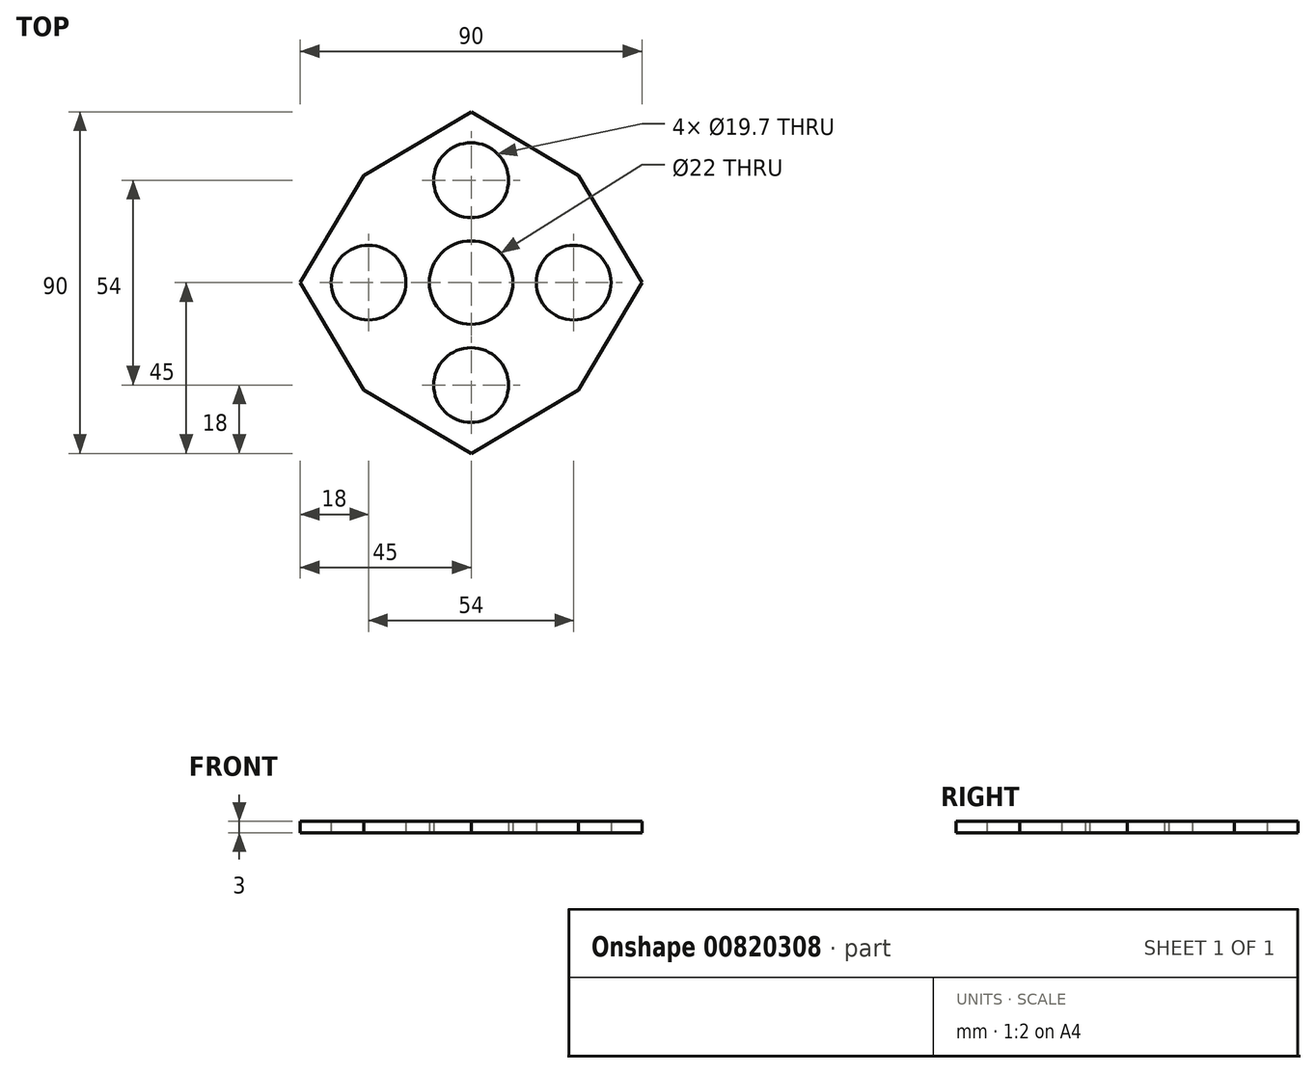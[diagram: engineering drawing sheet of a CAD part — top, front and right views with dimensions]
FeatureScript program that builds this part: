
annotation { "Feature Type Name" : "Feature", "Feature Type Description" : "" }
export const myFeature = defineFeature(function(context is Context, id is Id, definition is map)
    precondition{}
    {
        {
            var Q0;
            Q0=qCreatedBy(makeId("Top.planeOp"),FACE);
            var sketch = newSketch(context, id + "F0", { "sketchPlane" : qUnion([Q0])});
            skCircle(sketch, "E0", {"center": v(0, 0) * mm, "radius": 11 * mm});
            skLineSegment(sketch, "E1", {"start": v(-45, 0) * mm, "end": v(-28.28, 28.28) * mm});
            skLineSegment(sketch, "E2", {"start": v(-28.28, 28.28) * mm, "end": v(0, 45) * mm});
            skLineSegment(sketch, "E3", {"start": v(0, 45) * mm, "end": v(28.28, 28.28) * mm});
            skLineSegment(sketch, "E4", {"start": v(45, 0) * mm, "end": v(28.28, 28.28) * mm});
            skLineSegment(sketch, "E5", {"start": v(45, 0) * mm, "end": v(28.28, -28.28) * mm});
            skLineSegment(sketch, "E6", {"start": v(28.28, -28.28) * mm, "end": v(0, -45) * mm});
            skLineSegment(sketch, "E7", {"start": v(0, -45) * mm, "end": v(-28.28, -28.28) * mm});
            skLineSegment(sketch, "E8", {"start": v(-28.28, -28.28) * mm, "end": v(-45, 0) * mm});
            skCircle(sketch, "E9", {"center": v(0, 27) * mm, "radius": 9.85 * mm});
            skCircle(sketch, "E10", {"center": v(-27, 0) * mm, "radius": 9.85 * mm});
            skCircle(sketch, "E11", {"center": v(0, -27) * mm, "radius": 9.85 * mm});
            skCircle(sketch, "E12", {"center": v(27, 0) * mm, "radius": 9.85 * mm});
            skSolve(sketch);
        }
        {
            var Q0;
            Q0 = qSketchRegion(id + "F0", true);
            extrude(context, id + "F1", {"entities" : qUnion([Q0]), "depth" : 3 * mm, "offsetDistance" : 25 * mm});
        }
    });
